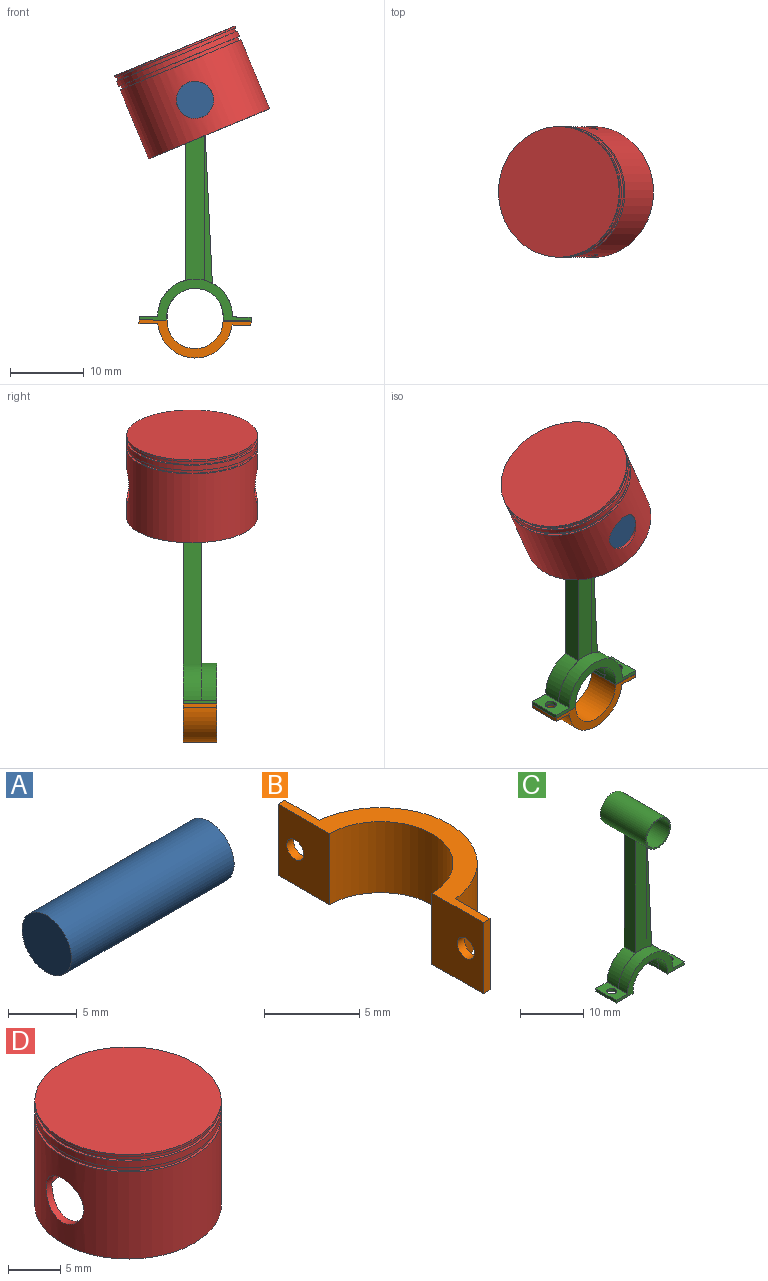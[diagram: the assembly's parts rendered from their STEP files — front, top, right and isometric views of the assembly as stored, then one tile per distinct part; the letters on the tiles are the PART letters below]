
ASSEMBLY  parts=4 mates=3
PART A: 3 faces, bbox 16.8x5.1x5.1 mm
  f0: cylinder r=2.54mm len=16.76mm, axis (-1,0,0), area 267.5mm2, adj f1,f2
  f1: plane 5.08x5.08mm, normal (1,0,0), area 20.3mm2, adj f0
  f2: plane 5.08x5.08mm, normal (-1,0,0), area 20.3mm2, adj f0
PART B: 12 faces, bbox 5.1x15.2x4.6 mm
  f0: plane 4.57x3.81mm, normal (-1,0,0), area 16.2mm2, adj f3,f5,f8,f9,f11
  f1: plane 4.57x3.81mm, normal (-1,0,0), area 16.2mm2, adj f3,f7,f8,f9,f10
  f2: cylinder r=5.08mm len=10.11mm, axis (0,0,1), area 68.3mm2, adj f4,f6,f8,f9
  f3: cylinder r=3.81mm len=7.62mm, axis (0,0,1), area 54.7mm2, adj f0,f1,f8,f9
  f4: plane 4.57x2.57mm, normal (1,0,0), area 10.5mm2, adj f2,f5,f8,f9,f11
  f5: plane 4.57x0.51mm, normal (0,1,0), area 2.3mm2, adj f0,f4,f8,f9
  f6: plane 4.57x2.57mm, normal (1,0,0), area 10.5mm2, adj f2,f7,f8,f9,f10
  f7: plane 4.57x0.51mm, normal (0,-1,0), area 2.3mm2, adj f1,f6,f8,f9
  f8: plane 15.24x5.08mm, normal (0,0,1), area 20.3mm2, adj f0,f1,f2,f3,f4,f5,f6,f7
  f9: plane 15.24x5.08mm, normal (0,0,-1), area 20.3mm2, adj f0,f1,f2,f3,f4,f5,f6,f7
  f10: cylinder r=0.64mm len=1.27mm, axis (1,0,0), area 2mm2, adj f1,f6
  f11: cylinder r=0.64mm len=1.27mm, axis (1,0,0), area 2mm2, adj f0,f4
PART C: 29 faces, bbox 15.2x10.2x32.9 mm
  f0: cylinder r=5.11mm len=10.22mm, axis (0,1,0), area 32.6mm2, adj f3,f18,f20,f23,f25,f26
  f1: plane 4.11x2.44mm, normal (0,-1,0), area 0.1mm2, adj f13,f14,f24
  f2: plane 4.29x3.39mm, normal (0,-1,0), area 0.1mm2, adj f13,f16,f24
  f3: plane 22.47x4.63mm, normal (0,-1,0), area 55.2mm2, adj f0,f4,f5,f7,f11,f12
  f4: plane 22.06x2.54mm, normal (1,0,0), area 56mm2, adj f3,f6,f7,f12
  f5: plane 22.06x2.54mm, normal (-1,0,0), area 56mm2, adj f3,f6,f7,f11
  f6: plane 27.6x15.25mm, normal (0,1,0), area 76.9mm2, adj f4,f5,f7,f11,f12,f13,f14,f15
  f7: cylinder r=2.79mm len=10.16mm, axis (0,1,0), area 171.7mm2, adj f3,f4,f5,f6,f8,f9
  f8: plane 5.59x5.59mm, normal (0,-1,0), area 4.2mm2, adj f7,f10
  f9: plane 5.59x5.59mm, normal (0,1,0), area 4.2mm2, adj f7,f10
  f10: cylinder r=2.54mm len=10.16mm, axis (0,-1,0), area 162.4mm2, adj f8,f9
  f11: cylinder r=5.08mm len=4.92mm, axis (0,1,0), area 17mm2, adj f3,f5,f6,f20,f26
  f12: cylinder r=5.08mm len=5mm, axis (0,1,0), area 17.2mm2, adj f3,f4,f6,f18,f23
  f13: cylinder r=3.81mm len=7.62mm, axis (0,1,0), area 30.6mm2, adj f1,f2,f6,f14,f16,f24
  f14: plane 2.54x0.51mm, normal (-1,0,0.02), area 1.3mm2, adj f1,f6,f13,f15
  f15: plane 4.57x3.81mm, normal (-0.02,0,-1), area 15.6mm2, adj f6,f14,f19,f24,f25,f28
  f16: plane 2.54x0.51mm, normal (1,0,-0.02), area 1.3mm2, adj f2,f6,f13,f17
  f17: plane 4.57x1.27mm, normal (0,0,-1), area 5.8mm2, adj f6,f16,f21,f24,f25
  f18: plane 4.57x2.54mm, normal (0.02,0,1), area 9.7mm2, adj f0,f6,f12,f19,f23,f25,f28
  f19: plane 4.57x0.51mm, normal (1,0,-0.02), area 2.3mm2, adj f6,f15,f18,f25
  f20: plane 4.57x2.54mm, normal (0.02,0,1), area 9.7mm2, adj f0,f6,f11,f22,f25,f26,f27
  f21: plane 4.57x2.54mm, normal (-0.02,0,-1), area 9.8mm2, adj f6,f17,f22,f25,f27
  f22: plane 4.57x0.51mm, normal (-1,0,0.02), area 2.3mm2, adj f6,f20,f21,f25
  f23: plane 4.58x2.76mm, normal (0,1,0), area 0.1mm2, adj f0,f12,f18
  f24: cylinder r=3.84mm len=7.69mm, axis (0,1,0), area 26.6mm2, adj f1,f2,f13,f15,f17,f25
  f25: plane 15.25x5.71mm, normal (0,-1,0), area 21.7mm2, adj f0,f15,f17,f18,f19,f20,f21,f22
  f26: plane 4.54x2.83mm, normal (0,1,0), area 0.1mm2, adj f0,f11,f20
  f27: cylinder r=0.76mm len=1.53mm, axis (0.02,0,1), area 2.4mm2, adj f20,f21
  f28: cylinder r=0.76mm len=1.53mm, axis (0.02,0,1), area 2.4mm2, adj f15,f18
PART D: 15 faces, bbox 17.8x17.8x12.2 mm
  f0: cylinder r=2.54mm len=5.08mm, axis (1,0,0), area 12.4mm2, adj f2,f13
  f1: cylinder r=8.89mm len=17.78mm, axis (0,0,-1), area 14.2mm2, adj f3,f12
  f2: cylinder r=8.89mm len=17.78mm, axis (0,0,1), area 526.5mm2, adj f0,f9,f10,f11
  f3: plane 17.78x17.78mm, normal (0,0,-1), area 14mm2, adj f1,f4
  f4: cylinder r=8.64mm len=17.27mm, axis (0,0,1), area 27.6mm2, adj f3,f7
  f5: cylinder r=8.89mm len=17.78mm, axis (0,0,1), area 42.6mm2, adj f6,f7
  f6: plane 17.78x17.78mm, normal (0,0,-1), area 14mm2, adj f5,f8
  f7: plane 17.78x17.78mm, normal (0,0,1), area 14mm2, adj f4,f5
  f8: cylinder r=8.64mm len=17.27mm, axis (0,0,1), area 27.6mm2, adj f6,f10
  f9: plane 17.78x17.78mm, normal (0,0,-1), area 40.7mm2, adj f2,f13
  f10: plane 17.78x17.78mm, normal (0,0,1), area 14mm2, adj f2,f8
  f11: cylinder r=2.54mm len=5.08mm, axis (1,0,0), area 12.4mm2, adj f2,f13
  f12: plane 17.78x17.78mm, normal (0,0,1), area 248.3mm2, adj f1
  f13: cylinder r=8.13mm len=16.26mm, axis (0,0,-1), area 413mm2, adj f0,f9,f11,f14
  f14: plane 16.26x16.26mm, normal (0,0,-1), area 207.5mm2, adj f13
PLACE A rot(axis=(0,0,-1),90deg) t=(-10.73,-1.52,11.33)mm
PLACE B rot(axis=(-0.57,0.58,0.58),120.5deg) t=(-10.74,-12.19,-18.73)mm
PLACE C t=(-10.73,-9.9,11.33)mm
PLACE D rot(axis=(0.19,-0.19,-0.96),92.2deg) t=(-13.39,-9.82,17.73)mm
MATE revolute A.f0 <-> D.f0  axis (0,1,0) through (-10.73,-1.52,11.33)mm
MATE fastened B.f11 <-> C.f27  axis (0.02,0,1) through (-17.07,-10.92,-18.62)mm
MATE fastened A.f0 <-> C.f7  axis (0,1,0) through (-10.73,-9.9,11.33)mm
